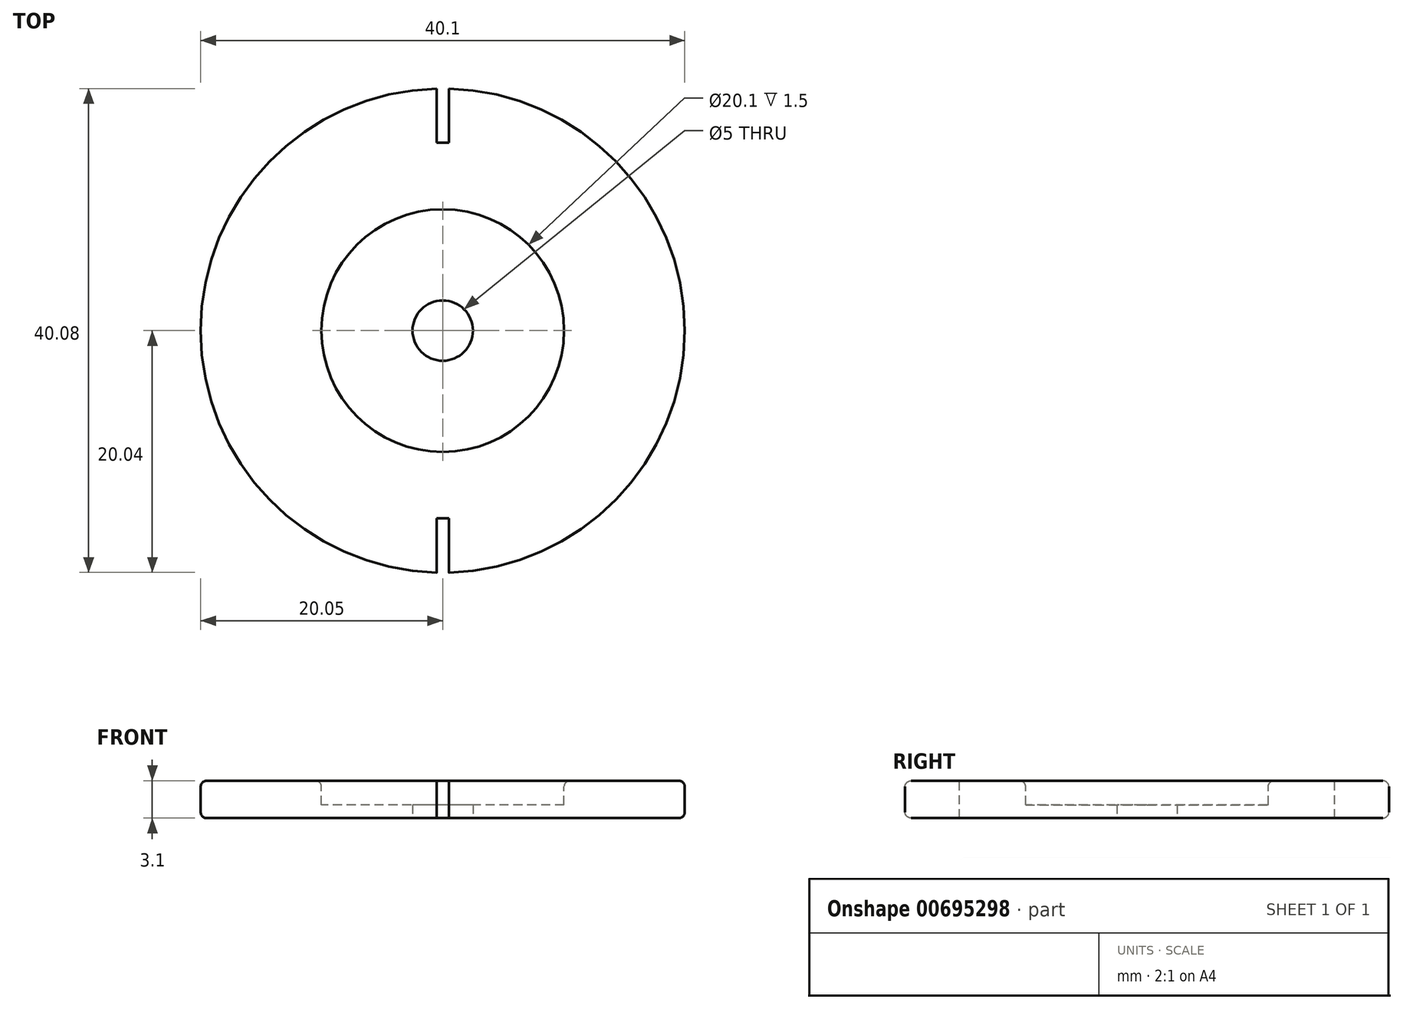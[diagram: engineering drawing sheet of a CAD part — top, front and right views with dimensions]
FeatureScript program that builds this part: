
annotation { "Feature Type Name" : "Feature", "Feature Type Description" : "" }
export const myFeature = defineFeature(function(context is Context, id is Id, definition is map)
    precondition{}
    {
        {
            var Q0;
            Q0=qCreatedBy(makeId("Top.planeOp"),FACE);
            var sketch = newSketch(context, id + "F0", { "sketchPlane" : qUnion([Q0])});
            skCircle(sketch, "E0", {"center": v(0, 0) * mm, "radius": 20.05 * mm});
            skSolve(sketch);
        }
        {
            var Q0;
            Q0=qSketchRegion(id+"F0",true);
            extrude(context, id + "F1", {"entities" : qUnion([Q0]), "depth" : 3.1 * mm});
        }
        {
            var Q0;
            Q0=makeQuery(id+"F1.opExtrude","CAP_FACE",FACE,{"disambiguationData":[OSD([sQuery(id+"F0.wireOp",EDGE,"E0")])],"isStart":false});
            var sketch = newSketch(context, id + "F2", { "sketchPlane" : qUnion([Q0])});
            skCircle(sketch, "E1", {"center": v(0, 0) * mm, "radius": 10.05 * mm});
            skSolve(sketch);
        }
        {
            var Q0;
            Q0=qSketchRegion(id+"F2",true);
            extrude(context, id + "F3", {"entities" : qUnion([Q0]), "operationType" : NewBodyOperationType.REMOVE, "oppositeDirection" : true, "depth" : 2 * mm});
        }
        {
            var Q0;
            Q0=makeQuery(id+"F1.opExtrude","CAP_FACE",FACE,{"disambiguationData":[OSD([sQuery(id+"F0.wireOp",EDGE,"E0")])],"isStart":false});
            var Q1;
            Q1=makeQuery(id+"F1.opExtrude","CAP_FACE",FACE,{"disambiguationData":[OSD([sQuery(id+"F0.wireOp",EDGE,"E0")])],"isStart":true});
            fillet(context, id + "F4", {"entities" : qUnion([Q0, Q1]), "radius" : 0.5 * mm, "tangentPropagation" : true, "allowEdgeOverflow" : false});
        }
        {
            var Q0;
            Q0=makeQuery(id+"F1.opExtrude","CAP_FACE",FACE,{"disambiguationData":[OSD([sQuery(id+"F0.wireOp",EDGE,"E0")])],"isStart":true});
            var sketch = newSketch(context, id + "F5", { "sketchPlane" : qUnion([Q0])});
            skCircle(sketch, "E2", {"center": v(0, 0) * mm, "radius": 2.5 * mm});
            skSolve(sketch);
        }
        {
            var Q0;
            Q0=qSketchRegion(id+"F5",true);
            extrude(context, id + "F6", {"entities" : qUnion([Q0]), "operationType" : NewBodyOperationType.REMOVE, "endBound" : BoundingType.THROUGH_ALL, "oppositeDirection" : true, "depth" : 25 * mm});
        }
        {
            var Q0;
            Q0=makeQuery(id+"F1.opExtrude","CAP_FACE",FACE,{"disambiguationData":[OSD([sQuery(id+"F0.wireOp",EDGE,"E0")])],"isStart":false});
            var sketch = newSketch(context, id + "F7", { "sketchPlane" : qUnion([Q0])});
            skLineSegment(sketch, "E3.bottom", {"start": v(-0.5, 20.55) * mm, "end": v(0.5, 20.55) * mm});
            skLineSegment(sketch, "E3.top", {"start": v(-0.5, 15.55) * mm, "end": v(0.5, 15.55) * mm});
            skLineSegment(sketch, "E3.left", {"start": v(-0.5, 20.55) * mm, "end": v(-0.5, 15.55) * mm});
            skLineSegment(sketch, "E3.right", {"start": v(0.5, 20.55) * mm, "end": v(0.5, 15.55) * mm});
            skPoint(sketch, "E3.middle", {"position": v(0, 18.05) * mm});
            skLineSegment(sketch, "E4.MirrorCS", {"start": v(-0.5, -15.55) * mm, "end": v(0.5, -15.55) * mm});
            skLineSegment(sketch, "E5.MirrorCS", {"start": v(-0.5, -20.55) * mm, "end": v(0.5, -20.55) * mm});
            skLineSegment(sketch, "E6.MirrorCS", {"start": v(-0.5, -20.55) * mm, "end": v(-0.5, -15.55) * mm});
            skPoint(sketch, "E7.MirrorP", {"position": v(0, -18.05) * mm});
            skLineSegment(sketch, "E8.MirrorCS", {"start": v(0.5, -20.55) * mm, "end": v(0.5, -15.55) * mm});
            skSolve(sketch);
        }
        {
            var Q0;
            Q0=qSketchRegion(id+"F7",true);
            extrude(context, id + "F8", {"entities" : qUnion([Q0]), "operationType" : NewBodyOperationType.REMOVE, "endBound" : BoundingType.THROUGH_ALL, "oppositeDirection" : true, "depth" : 25 * mm, "offsetDistance" : 25 * mm});
        }
    });
